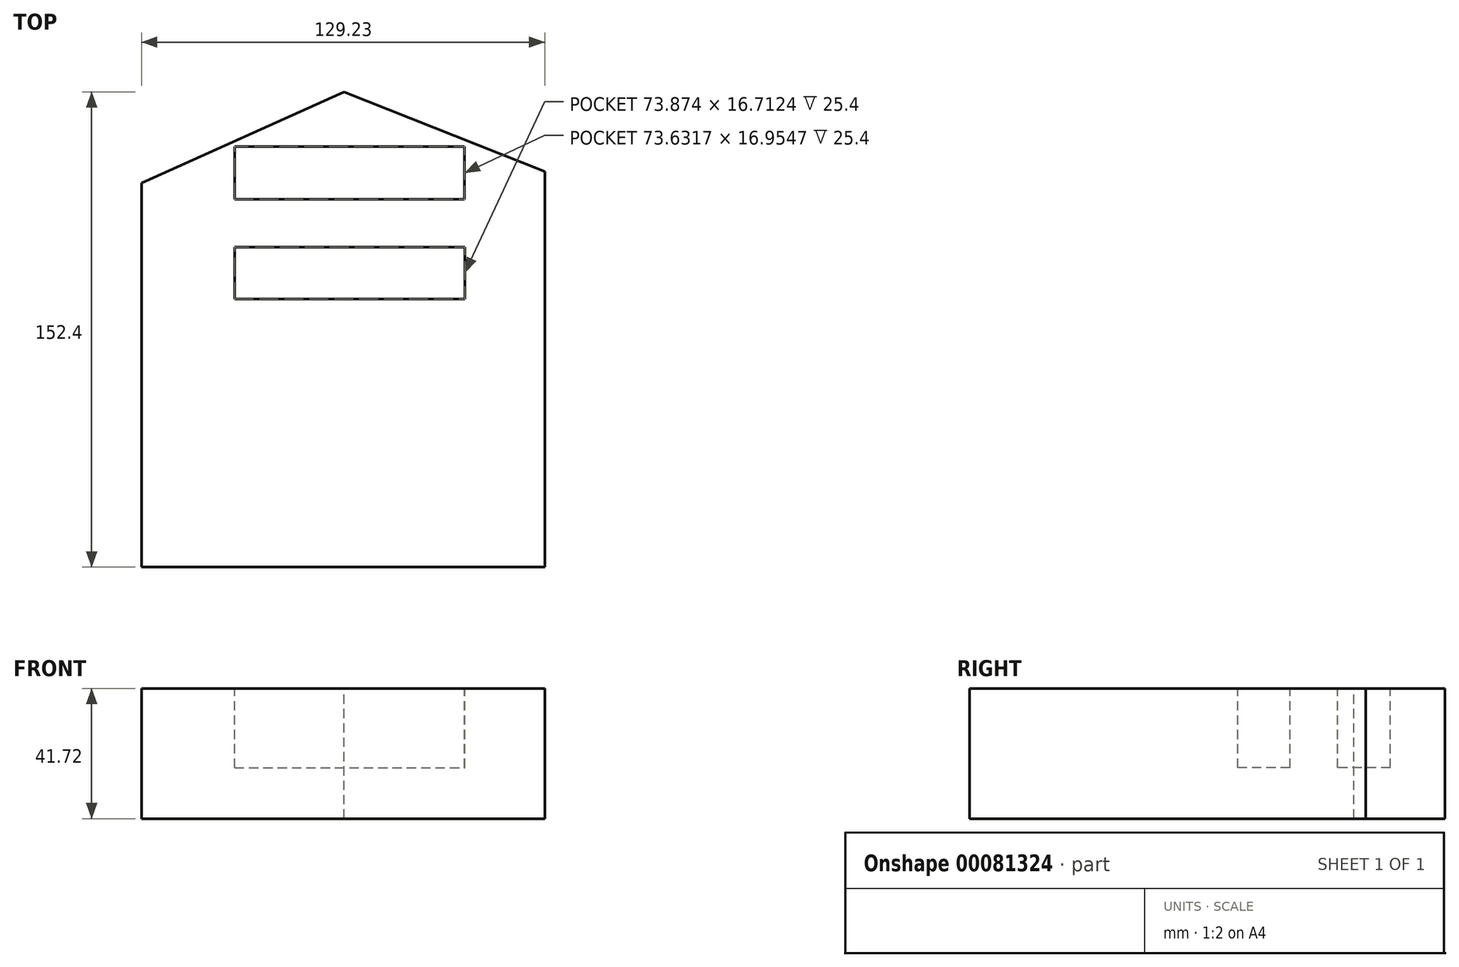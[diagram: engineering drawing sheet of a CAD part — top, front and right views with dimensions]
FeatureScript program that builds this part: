
annotation { "Feature Type Name" : "Feature", "Feature Type Description" : "" }
export const myFeature = defineFeature(function(context is Context, id is Id, definition is map)
    precondition{}
    {
        {
            var Q0;
            Q0=qCreatedBy(makeId("Front.planeOp"),FACE);
            var sketch = newSketch(context, id + "F0", { "sketchPlane" : qUnion([Q0])});
            skLineSegment(sketch, "E0.bottom", {"start": v(-64.92, 14.45) * mm, "end": v(64.3, 14.45) * mm});
            skLineSegment(sketch, "E0.top", {"start": v(-64.92, -27.27) * mm, "end": v(64.3, -27.27) * mm});
            skLineSegment(sketch, "E0.left", {"start": v(-64.92, 14.45) * mm, "end": v(-64.92, -27.27) * mm});
            skLineSegment(sketch, "E0.right", {"start": v(64.3, 14.45) * mm, "end": v(64.3, -27.27) * mm});
            skSolve(sketch);
        }
        {
            var Q0;
            Q0=makeQuery(id+"F0.imprint","IMPRINT",FACE,{"disambiguationData":[TD([[makeQuery(id+"F0.imprint","IMPRINT",EDGE,{"derivedFrom":sQuery(id+"F0.wireOp",EDGE,"E0.bottom")}),-1.0]])]});
            extrude(context, id + "F1", {"entities" : qUnion([Q0]), "depth" : 152.4 * mm});
        }
        {
            var Q0;
            Q0=makeQuery(id+"F1.opExtrude","SWEPT_FACE",FACE,{"disambiguationData":[OSD([sQuery(id+"F0.wireOp",EDGE,"E0.bottom")])]});
            var sketch = newSketch(context, id + "F2", { "sketchPlane" : qUnion([Q0])});
            skLineSegment(sketch, "E1.bottom", {"start": v(-35.12, -17.51) * mm, "end": v(38.51, -17.51) * mm});
            skLineSegment(sketch, "E1.top", {"start": v(-35.12, -34.47) * mm, "end": v(38.51, -34.47) * mm});
            skLineSegment(sketch, "E1.left", {"start": v(-35.12, -17.51) * mm, "end": v(-35.12, -34.47) * mm});
            skLineSegment(sketch, "E1.right", {"start": v(38.51, -17.51) * mm, "end": v(38.51, -34.47) * mm});
            skLineSegment(sketch, "E2.bottom", {"start": v(-35.12, -49.73) * mm, "end": v(38.75, -49.73) * mm});
            skLineSegment(sketch, "E2.top", {"start": v(-35.12, -66.44) * mm, "end": v(38.75, -66.44) * mm});
            skLineSegment(sketch, "E2.left", {"start": v(-35.12, -49.73) * mm, "end": v(-35.12, -66.44) * mm});
            skLineSegment(sketch, "E2.right", {"start": v(38.75, -49.73) * mm, "end": v(38.75, -66.44) * mm});
            skSolve(sketch);
        }
        {
            var Q0;
            Q0=makeQuery(id+"F2.imprint","IMPRINT",FACE,{"disambiguationData":[TD([[makeQuery(id+"F2.imprint","IMPRINT",EDGE,{"derivedFrom":sQuery(id+"F2.wireOp",EDGE,"E1.bottom")}),-1.0]])]});
            var Q1;
            Q1=makeQuery(id+"F2.imprint","IMPRINT",FACE,{"disambiguationData":[TD([[makeQuery(id+"F2.imprint","IMPRINT",EDGE,{"derivedFrom":sQuery(id+"F2.wireOp",EDGE,"E2.bottom")}),-1.0]])]});
            extrude(context, id + "F3", {"entities" : qUnion([Q0, Q1]), "operationType" : NewBodyOperationType.REMOVE, "oppositeDirection" : true, "depth" : 25.4 * mm});
        }
        {
            var Q0;
            Q0=makeQuery(id+"F1.opExtrude","SWEPT_FACE",FACE,{"disambiguationData":[OSD([sQuery(id+"F0.wireOp",EDGE,"E0.bottom")])]});
            var sketch = newSketch(context, id + "F4", { "sketchPlane" : qUnion([Q0])});
            skLineSegment(sketch, "E3", {"start": v(-64.92, -29.2) * mm, "end": v(0, 0) * mm});
            skLineSegment(sketch, "E4", {"start": v(0, 0) * mm, "end": v(64.3, -25.48) * mm});
            skSolve(sketch);
        }
        {
            var Q0;
            {var subQ0=sQuery(id+"F4.wireOp",EDGE,"E4");Q0=makeQuery(id+"F4.imprint","IMPRINT",FACE,{"disambiguationData":[TD([[makeQuery(id+"F4.imprint","IMPRINT",EDGE,{"derivedFrom":subQ0}),1.0]])]});}
            var Q1;
            {var subQ0=sQuery(id+"F4.wireOp",EDGE,"E3");Q1=makeQuery(id+"F4.imprint","IMPRINT",FACE,{"disambiguationData":[TD([[makeQuery(id+"F4.imprint","IMPRINT",EDGE,{"derivedFrom":subQ0}),1.0]])]});}
            extrude(context, id + "F5", {"entities" : qUnion([Q0, Q1]), "operationType" : NewBodyOperationType.REMOVE, "endBound" : BoundingType.THROUGH_ALL, "oppositeDirection" : true, "depth" : 25.4 * mm});
        }
    });
